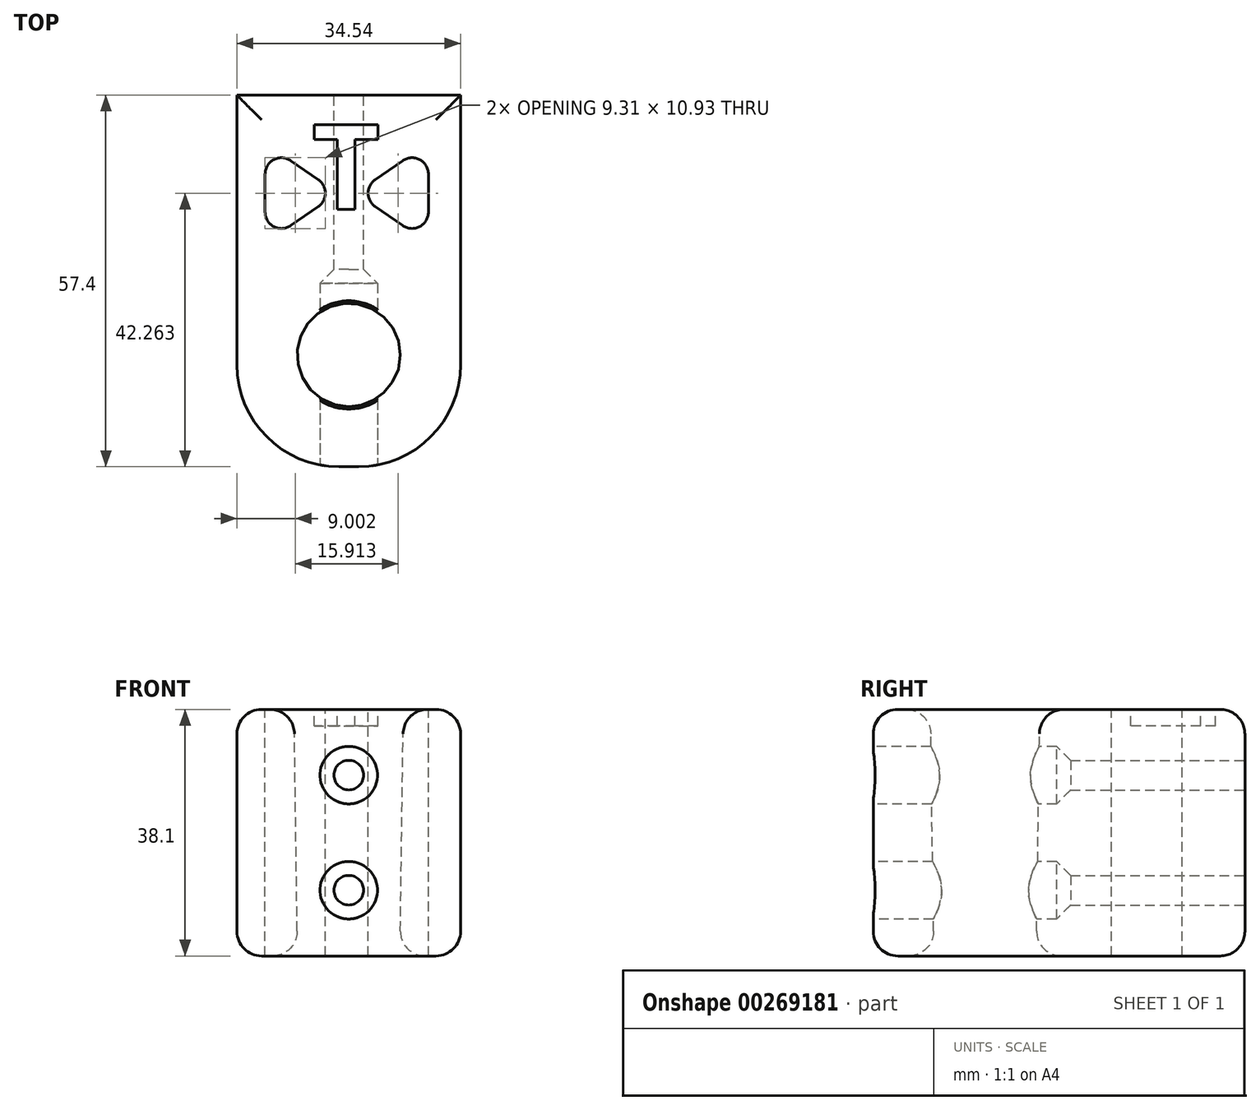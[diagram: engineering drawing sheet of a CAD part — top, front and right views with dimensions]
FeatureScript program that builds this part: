
annotation { "Feature Type Name" : "Feature", "Feature Type Description" : "" }
export const myFeature = defineFeature(function(context is Context, id is Id, definition is map)
    precondition{}
    {
        {
            var Q0;
            Q0=qCreatedBy(makeId("Top.planeOp"),FACE);
            var sketch = newSketch(context, id + "F0", { "sketchPlane" : qUnion([Q0])});
            skLineSegment(sketch, "E0.bottom", {"start": v(0, 0) * mm, "end": v(34.54, 0) * mm});
            skLineSegment(sketch, "E0.top", {"start": v(0, -34.54) * mm, "end": v(34.54, -34.54) * mm});
            skLineSegment(sketch, "E0.left", {"start": v(0, 0) * mm, "end": v(0, -34.54) * mm});
            skLineSegment(sketch, "E0.right", {"start": v(34.54, 0) * mm, "end": v(34.54, -34.54) * mm});
            skSolve(sketch);
        }
        {
            var Q0;
            Q0=qSketchRegion(id+"F0",true);
            extrude(context, id + "F1", {"entities" : qUnion([Q0]), "depth" : 38.1 * mm});
        }
        {
            var Q0;
            Q0=makeQuery(id+"F1.opExtrude","CAP_FACE",FACE,{"disambiguationData":[OSD([sQuery(id+"F0.wireOp",EDGE,"E0.bottom"),sQuery(id+"F0.wireOp",EDGE,"E0.top"),sQuery(id+"F0.wireOp",EDGE,"E0.left"),sQuery(id+"F0.wireOp",EDGE,"E0.right")])],"isStart":false});
            var sketch = newSketch(context, id + "F2", { "sketchPlane" : qUnion([Q0])});
            skCircle(sketch, "E1", {"center": v(17.27, -17.27) * mm, "radius": 8.45 * mm});
            skPoint(sketch, "E1.centerSnap0", {"position": v(17.27, -34.54) * mm});
            skPoint(sketch, "E1.centerSnap1", {"position": v(34.54, -17.27) * mm});
            skSolve(sketch);
        }
        {
            var Q0;
            Q0=makeQuery(id+"F1.opExtrude","SWEPT_EDGE",EDGE,{"disambiguationData":[OSD([sQuery(id+"F0.wireOp",EDGE,"E0.top"),sQuery(id+"F0.wireOp",EDGE,"E0.right")])]});
            var Q1;
            Q1=makeQuery(id+"F1.opExtrude","SWEPT_EDGE",EDGE,{"disambiguationData":[OSD([sQuery(id+"F0.wireOp",EDGE,"E0.bottom"),sQuery(id+"F0.wireOp",EDGE,"E0.right")])]});
            fillet(context, id + "F3", {"entities" : qUnion([Q0, Q1]), "radius" : 15.75 * mm, "tangentPropagation" : true, "allowEdgeOverflow" : false});
        }
        {
            var Q0;
            Q0=makeQuery(id+"F1.opExtrude","SWEPT_FACE",FACE,{"disambiguationData":[OSD([sQuery(id+"F0.wireOp",EDGE,"E0.left")])]});
            var sketch = newSketch(context, id + "F4", { "sketchPlane" : qUnion([Q0])});
            skCircle(sketch, "E2", {"center": v(17.27, 10.16) * mm, "radius": 2.29 * mm});
            skPoint(sketch, "E2.centerSnap0", {"position": v(17.27, 0) * mm});
            skCircle(sketch, "E3", {"center": v(17.27, 27.94) * mm, "radius": 2.29 * mm});
            skPoint(sketch, "E3.centerSnap0", {"position": v(17.27, 38.1) * mm});
            skSolve(sketch);
        }
        {
            var Q0;
            Q0=qSketchRegion(id+"F4",true);
            extrude(context, id + "F5", {"entities" : qUnion([Q0]), "operationType" : NewBodyOperationType.REMOVE, "endBound" : BoundingType.THROUGH_ALL, "oppositeDirection" : true, "depth" : 25.4 * mm});
        }
        {
            var Q0;
            {var subQ0=sQuery(id+"F0.wireOp",EDGE,"E0.right");Q0=makeQuery(id+"F5.boolean.opBoolean","SPLIT",FACE,{"disambiguationData":[TD([makeQuery(id+"F3.opFillet","BLEND_FACE",FACE,{"disambiguationData":[OSD([sQuery(id+"F0.wireOp",EDGE,"E0.bottom"),subQ0])]}),makeQuery(id+"F3.opFillet","BLEND_FACE",FACE,{"disambiguationData":[OSD([sQuery(id+"F0.wireOp",EDGE,"E0.top"),subQ0])]}),makeQuery(id+"F5.opExtrude","SWEPT_FACE",FACE,{"disambiguationData":[OSD([sQuery(id+"F4.wireOp",EDGE,"E2")])]}),makeQuery(id+"F5.opExtrude","SWEPT_FACE",FACE,{"disambiguationData":[OSD([sQuery(id+"F4.wireOp",EDGE,"E3")])]})])],"derivedFrom":makeQuery(id+"F1.opExtrude","SWEPT_FACE",FACE,{"disambiguationData":[OSD([subQ0])]})});}
            var sketch = newSketch(context, id + "F6", { "sketchPlane" : qUnion([Q0])});
            skCircle(sketch, "E4", {"center": v(-17.27, 27.94) * mm, "radius": 4.45 * mm});
            skCircle(sketch, "E5", {"center": v(-17.27, 10.16) * mm, "radius": 4.45 * mm});
            skSolve(sketch);
        }
        {
            var Q0;
            Q0=qSketchRegion(id+"F6",true);
            extrude(context, id + "F7", {"entities" : qUnion([Q0]), "operationType" : NewBodyOperationType.REMOVE, "oppositeDirection" : true, "depth" : 27.94 * mm});
        }
        {
            var Q0;
            Q0=makeQuery(id+"F7.boolean.opBoolean","INTERSECT",EDGE,{"derivedFrom":[makeQuery(id+"F5.boolean.opBoolean","COPY",FACE,{"disambiguationData":[TD([makeQuery(id+"F1.opExtrude","SWEPT_FACE",FACE,{"disambiguationData":[OSD([sQuery(id+"F0.wireOp",EDGE,"E0.left")])]})])],"derivedFrom":makeQuery(id+"F5.opExtrude","SWEPT_FACE",FACE,{"disambiguationData":[OSD([sQuery(id+"F4.wireOp",EDGE,"E3")])]})}),makeQuery(id+"F7.opExtrude","CAP_FACE",FACE,{"disambiguationData":[OSD([sQuery(id+"F6.wireOp",EDGE,"E4")])],"isStart":false})]});
            var Q1;
            Q1=makeQuery(id+"F7.boolean.opBoolean","INTERSECT",EDGE,{"derivedFrom":[makeQuery(id+"F5.boolean.opBoolean","COPY",FACE,{"disambiguationData":[TD([makeQuery(id+"F1.opExtrude","SWEPT_FACE",FACE,{"disambiguationData":[OSD([sQuery(id+"F0.wireOp",EDGE,"E0.left")])]})])],"derivedFrom":makeQuery(id+"F5.opExtrude","SWEPT_FACE",FACE,{"disambiguationData":[OSD([sQuery(id+"F4.wireOp",EDGE,"E2")])]})}),makeQuery(id+"F7.opExtrude","CAP_FACE",FACE,{"disambiguationData":[OSD([sQuery(id+"F6.wireOp",EDGE,"E5")])],"isStart":false})]});
            chamfer(context, id + "F8", {"entities" : qUnion([Q0, Q1]), "width" : 2.54 * mm, "tangentPropagation" : true});
        }
        {
            var Q0;
            Q0=makeQuery(id+"F1.opExtrude","SWEPT_FACE",FACE,{"disambiguationData":[OSD([sQuery(id+"F0.wireOp",EDGE,"E0.left")])]});
            extrude(context, id + "F9", {"entities" : qUnion([Q0]), "operationType" : NewBodyOperationType.ADD, "depth" : 22.86 * mm});
        }
        {
            var Q0;
            Q0=qSketchRegion(id+"F2",true);
            extrude(context, id + "F10", {"entities" : qUnion([Q0]), "operationType" : NewBodyOperationType.REMOVE, "endBound" : BoundingType.THROUGH_ALL, "oppositeDirection" : true, "depth" : 25.4 * mm, "hasDraft" : true, "draftAngle" : .8 * degree, "draftPullDirection" : true});
        }
        {
            var Q0;
            Q0=makeQuery(id+"F1.opExtrude","CAP_FACE",FACE,{"disambiguationData":[OSD([sQuery(id+"F0.wireOp",EDGE,"E0.bottom"),sQuery(id+"F0.wireOp",EDGE,"E0.top"),sQuery(id+"F0.wireOp",EDGE,"E0.left"),sQuery(id+"F0.wireOp",EDGE,"E0.right")])],"isStart":false});
            fillet(context, id + "F11", {"entities" : qUnion([Q0]), "radius" : 3.8 * mm, "tangentPropagation" : true, "allowEdgeOverflow" : false});
        }
        {
            var Q0;
            Q0=makeQuery(id+"F1.opExtrude","CAP_FACE",FACE,{"disambiguationData":[OSD([sQuery(id+"F0.wireOp",EDGE,"E0.bottom"),sQuery(id+"F0.wireOp",EDGE,"E0.top"),sQuery(id+"F0.wireOp",EDGE,"E0.left"),sQuery(id+"F0.wireOp",EDGE,"E0.right")])],"isStart":true});
            fillet(context, id + "F12", {"entities" : qUnion([Q0]), "radius" : 3.8 * mm, "tangentPropagation" : true, "allowEdgeOverflow" : false});
        }
        {
            var Q0;
            Q0=makeQuery(id+"F1.opExtrude","SWEPT_BODY",BODY,{"disambiguationData":[OSD([sQuery(id+"F0.wireOp",EDGE,"E0.bottom"),sQuery(id+"F0.wireOp",EDGE,"E0.top"),sQuery(id+"F0.wireOp",EDGE,"E0.left"),sQuery(id+"F0.wireOp",EDGE,"E0.right")])]});
            var Q1;
            Q1=makeQuery(id+"F9.opExtrude","CAP_EDGE",EDGE,{"disambiguationData":[OSD([sQuery(id+"F0.wireOp",EDGE,"E0.bottom"),sQuery(id+"F0.wireOp",EDGE,"E0.left")])],"isStart":false});
            transform(context, id + "F13", {"entities" : qUnion([Q0]), "transformType" : TransformType.ROTATION, "transformAxis" : qUnion([Q1]), "angle" : 90 * degree, "makeCopy" : false});
        }
        {
            var Q0;
            {var subQ0=sQuery(id+"F0.wireOp",EDGE,"E0.left");Q0=makeQuery(id+"F9.boolean.opBoolean","MERGE",FACE,{"derivedFrom":[makeQuery(id+"F1.opExtrude","CAP_FACE",FACE,{"disambiguationData":[OSD([sQuery(id+"F0.wireOp",EDGE,"E0.bottom"),sQuery(id+"F0.wireOp",EDGE,"E0.top"),subQ0,sQuery(id+"F0.wireOp",EDGE,"E0.right")])],"isStart":false}),makeQuery(id+"F9.opExtrude","SWEPT_FACE",FACE,{"disambiguationData":[OSD([subQ0]),TDD([makeQuery(id+"F1.opExtrude","CAP_EDGE",EDGE,{"disambiguationData":[OSD([subQ0])],"isStart":false})])]})]});}
            var sketch = newSketch(context, id + "F14", { "sketchPlane" : qUnion([Q0])});
            skLineSegment(sketch, "E6", {"start": v(-31.82, -10.12) * mm, "end": v(-36.05, -13.05) * mm});
            skLineSegment(sketch, "E7", {"start": v(-27.83, -12.2) * mm, "end": v(-27.83, -18.06) * mm});
            skLineSegment(sketch, "E8", {"start": v(-31.82, -20.15) * mm, "end": v(-36.05, -17.23) * mm});
            skArc(sketch, "E9.filletArc", {"start": v(-27.83, -12.2) * mm, "mid": v(-29.2, -9.96) * mm, "end": v(-31.82, -10.12) * mm});
            skArc(sketch, "E10.filletArc", {"start": v(-31.82, -20.15) * mm, "mid": v(-29.2, -20.31) * mm, "end": v(-27.83, -18.06) * mm});
            skArc(sketch, "E11.filletArc", {"start": v(-36.05, -13.05) * mm, "mid": v(-37.14, -15.14) * mm, "end": v(-36.05, -17.23) * mm});
            skLineSegment(sketch, "E12", {"start": v(-49.07, -20.15) * mm, "end": v(-44.84, -17.23) * mm});
            skLineSegment(sketch, "E13", {"start": v(-53.05, -18.06) * mm, "end": v(-53.05, -12.2) * mm});
            skLineSegment(sketch, "E14", {"start": v(-49.07, -10.12) * mm, "end": v(-44.84, -13.05) * mm});
            skArc(sketch, "E15.filletArc", {"start": v(-53.05, -18.06) * mm, "mid": v(-51.7, -20.31) * mm, "end": v(-49.07, -20.15) * mm});
            skArc(sketch, "E16.filletArc", {"start": v(-49.07, -10.12) * mm, "mid": v(-51.7, -9.96) * mm, "end": v(-53.05, -12.2) * mm});
            skArc(sketch, "E17.filletArc", {"start": v(-44.84, -17.23) * mm, "mid": v(-43.74, -15.14) * mm, "end": v(-44.84, -13.05) * mm});
            skLineSegment(sketch, "E18", {"start": v(-40.13, -3.81) * mm, "end": v(-40.13, -27.93) * mm, "construction": true});
            skLineSegment(sketch, "E19", {"start": v(-40.13, -15.87) * mm, "end": v(-26.67, -15.78) * mm, "construction": true});
            skLineSegment(sketch, "E20", {"start": v(-40.13, -27.93) * mm, "end": v(-22.86, -27.93) * mm, "construction": true});
            skLineSegment(sketch, "E21", {"start": v(-22.86, -27.93) * mm, "end": v(-57.4, -27.82) * mm, "construction": true});
            skPoint(sketch, "E22", {"position": v(-53.05, -15.14) * mm});
            skPoint(sketch, "E23", {"position": v(-27.83, -17.23) * mm});
            skSolve(sketch);
        }
        {
            var Q0;
            Q0=qSketchRegion(id+"F14",true);
            extrude(context, id + "F15", {"entities" : qUnion([Q0]), "operationType" : NewBodyOperationType.REMOVE, "endBound" : BoundingType.THROUGH_ALL, "oppositeDirection" : true, "depth" : 25.4 * mm});
        }
        {
            var Q0;
            {var subQ0=sQuery(id+"F0.wireOp",EDGE,"E0.left");Q0=makeQuery(id+"F9.boolean.opBoolean","MERGE",FACE,{"derivedFrom":[makeQuery(id+"F1.opExtrude","CAP_FACE",FACE,{"disambiguationData":[OSD([sQuery(id+"F0.wireOp",EDGE,"E0.bottom"),sQuery(id+"F0.wireOp",EDGE,"E0.top"),subQ0,sQuery(id+"F0.wireOp",EDGE,"E0.right")])],"isStart":false}),makeQuery(id+"F9.opExtrude","SWEPT_FACE",FACE,{"disambiguationData":[OSD([subQ0]),TDD([makeQuery(id+"F1.opExtrude","CAP_EDGE",EDGE,{"disambiguationData":[OSD([subQ0])],"isStart":false})])]})]});}
            var sketch = newSketch(context, id + "F16", { "sketchPlane" : qUnion([Q0])});
            skText(sketch, "E24", { "text": "T", "fontName": "OpenSans-Bold.ttf"});
            skLineSegment(sketch, "E25", {"start": v(-40.13, -3.81) * mm, "end": v(-40.13, -20.1) * mm, "construction": true});
            const initialGuessF16  = {"E24": [-0.04585, -0.01764, 1, 0, 0.0132]};
            skSetInitialGuess(sketch, initialGuessF16);
            skSolve(sketch);
        }
        {
            var Q0;
            Q0=qSketchRegion(id+"F16",true);
            extrude(context, id + "F17", {"entities" : qUnion([Q0]), "operationType" : NewBodyOperationType.REMOVE, "oppositeDirection" : true, "depth" : 2.54 * mm});
        }
    });
